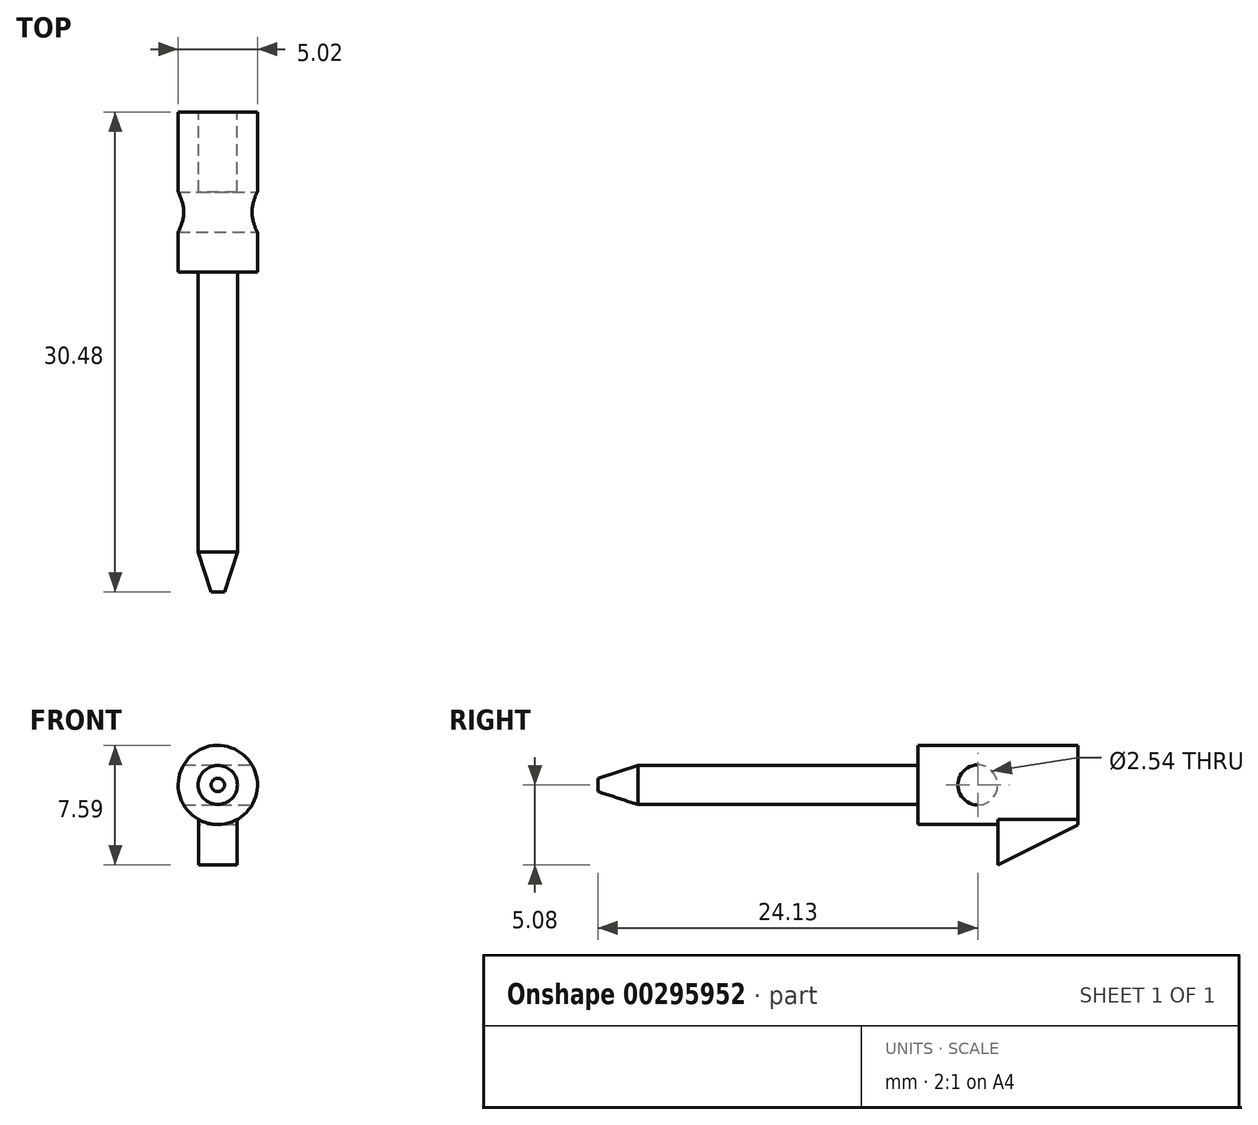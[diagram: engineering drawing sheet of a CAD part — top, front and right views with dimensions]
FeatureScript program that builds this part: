
annotation { "Feature Type Name" : "Feature", "Feature Type Description" : "" }
export const myFeature = defineFeature(function(context is Context, id is Id, definition is map)
    precondition{}
    {
        {
            var Q0;
            Q0=qCreatedBy(makeId("Front.planeOp"),FACE);
            var sketch = newSketch(context, id + "F0", { "sketchPlane" : qUnion([Q0])});
            skCircle(sketch, "E0", {"center": v(0, 0) * mm, "radius": 2.51 * mm});
            skSolve(sketch);
        }
        {
            var Q0;
            Q0=makeQuery(id+"F0.imprint","IMPRINT",FACE,{"disambiguationData":[TD([[makeQuery(id+"F0.imprint","IMPRINT",EDGE,{"derivedFrom":sQuery(id+"F0.wireOp",EDGE,"E0")}),1.0]])]});
            extrude(context, id + "F1", {"entities" : qUnion([Q0]), "depth" : 10.16 * mm});
        }
        {
            var Q0;
            Q0=makeQuery(id+"F1.opExtrude","CAP_FACE",FACE,{"disambiguationData":[OSD([sQuery(id+"F0.wireOp",EDGE,"E0")])],"isStart":false});
            var sketch = newSketch(context, id + "F2", { "sketchPlane" : qUnion([Q0])});
            skCircle(sketch, "E1", {"center": v(0, 0) * mm, "radius": 1.24 * mm});
            skSolve(sketch);
        }
        {
            var Q0;
            Q0 = qSketchRegion(id + "F2", true);
            var Q1;
            Q1=makeQuery(id+"F2.imprint","IMPRINT",FACE,{"disambiguationData":[TD([[makeQuery(id+"F2.imprint","IMPRINT",EDGE,{"derivedFrom":sQuery(id+"F2.wireOp",EDGE,"E1")}),1.0]])]});
            extrude(context, id + "F3", {"entities" : qUnion([Q0, Q1]), "operationType" : NewBodyOperationType.ADD, "depth" : 17.78 * mm});
        }
        {
            var Q0;
            Q0=makeQuery(id+"F3.opExtrude","CAP_FACE",FACE,{"disambiguationData":[OSD([sQuery(id+"F2.wireOp",EDGE,"E1")])],"isStart":false});
            cPlane(context, id + "F4", {"entities" : qUnion([Q0]), "cplaneType" : CPlaneType.OFFSET, "offset" : 2.54 * mm, "width" : 152.4 * mm, "height" : 152.4 * mm});
        }
        {
            var Q0;
            Q0=qCreatedBy(id+"F4.planeOp",FACE);
            var sketch = newSketch(context, id + "F5", { "sketchPlane" : qUnion([Q0])});
            skCircle(sketch, "E2", {"center": v(0, 0) * mm, "radius": 0.42 * mm});
            skSolve(sketch);
        }
        {
            var Q1;
            Q1=makeQuery(id+"F3.opExtrude","CAP_FACE",FACE,{"disambiguationData":[OSD([sQuery(id+"F2.wireOp",EDGE,"E1")])],"isStart":false});
            var Q2;
            Q2=makeQuery(id+"F5.imprint","IMPRINT",FACE,{"disambiguationData":[TD([[makeQuery(id+"F5.imprint","IMPRINT",EDGE,{"derivedFrom":sQuery(id+"F5.wireOp",EDGE,"E2")}),1.0]])]});
            loft(context, id + "F6", {"operationType" : NewBodyOperationType.ADD, "sheetProfilesArray" : [{ "sheetProfileEntities" : qUnion([Q1]) }, { "sheetProfileEntities" : qUnion([Q2]) }]});
        }
        {
            var Q0;
            Q0=qCreatedBy(makeId("Right.planeOp"),FACE);
            var sketch = newSketch(context, id + "F7", { "sketchPlane" : qUnion([Q0])});
            skLineSegment(sketch, "E3", {"start": v(0, 0) * mm, "end": v(-6.35, 0) * mm});
            skCircle(sketch, "E4", {"center": v(-6.35, 0) * mm, "radius": 1.27 * mm});
            skSolve(sketch);
        }
        {
            var Q0;
            Q0 = qSketchRegion(id + "F7", true);
            extrude(context, id + "F8", {"entities" : qUnion([Q0]), "operationType" : NewBodyOperationType.REMOVE, "oppositeDirection" : true, "depth" : 25.4 * mm});
        }
        {
            var Q0;
            Q0 = qSketchRegion(id + "F7", true);
            extrude(context, id + "F9", {"entities" : qUnion([Q0]), "operationType" : NewBodyOperationType.REMOVE, "depth" : 25.4 * mm});
        }
        {
            var Q0;
            Q0=qCreatedBy(makeId("Right.planeOp"),FACE);
            var sketch = newSketch(context, id + "F10", { "sketchPlane" : qUnion([Q0])});
            skLineSegment(sketch, "E5", {"start": v(0, 0) * mm, "end": v(0, -2.54) * mm});
            skLineSegment(sketch, "E6", {"start": v(0, -2.54) * mm, "end": v(-5.08, -5.08) * mm});
            skLineSegment(sketch, "E7", {"start": v(-5.08, -5.08) * mm, "end": v(-5.08, -2.54) * mm});
            skLineSegment(sketch, "E8", {"start": v(-5.08, -2.54) * mm, "end": v(-5.08, 0) * mm});
            skLineSegment(sketch, "E9", {"start": v(-5.08, 0) * mm, "end": v(0, 0) * mm});
            skSolve(sketch);
        }
        {
            var Q0;
            Q0 = qSketchRegion(id + "F10", true);
            extrude(context, id + "F11", {"entities" : qUnion([Q0]), "operationType" : NewBodyOperationType.ADD, "depth" : 1.22 * mm});
        }
        {
            var Q0;
            Q0 = qSketchRegion(id + "F10", true);
            extrude(context, id + "F12", {"entities" : qUnion([Q0]), "operationType" : NewBodyOperationType.ADD, "oppositeDirection" : true, "depth" : 1.22 * mm});
        }
    });
